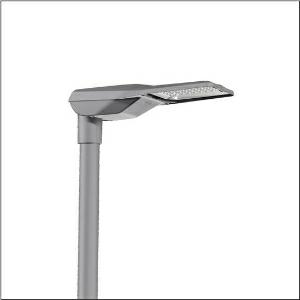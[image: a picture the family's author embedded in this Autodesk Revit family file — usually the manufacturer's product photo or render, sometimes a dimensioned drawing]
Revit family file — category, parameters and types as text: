
# Revit family: streetlight_sl_21_iq_mini___st1_5a_5xe2p41d08hb_72ee
name_source: partatom
category: Lighting Fixtures
units: mm (PartAtom-declared; Revit-internal decimal feet)

## family parameters
Cut with Voids When Loaded = No
Host = Face
Light Source = No
Part Type = Normal
Room Calculation Point = No
Round Connector Dimension = Use Diameter
Shared = No

## types (1)
- --- (1 x LED, 9690 lm, 70.9 W, 4000K)
    Apparent Load = 71 VA
    CIE Flux Codes = 22 53 95 100 100
    Color Rendering = 70
    Color Temperature = 4000K
    Default Elevation = 1800 mm
    Description = Streetlight SL 21 mini, mast luminaire, primary light control with lens, of PMMA, primary optical cover: cover, of toughened safety glass, transparent, light distribution: ST1.5a, light emission: direct distribution, primary light characteristic: asymmetric, installation type: post-top, side-entry, LED, High Power LED, rated luminous flux: 9.690lm, luminous efficacy: 137lm/W, light colour: 740, colour temperature: 4000K, control gear: ECG iQ, control: Auto-Match, Temp-Guard, Lumen-Switch, Night-Set, Smart-Wire, Light-Fading, Desk-Remote (wireless, voltage-free reading and setting of iQ features in the workshop via application-optimized NFC function/RFID function), optimised constant luminous flux control (CLO 2.0), mains connection: 220..240V, AC, 50/60Hz, start of lifetime: 71W, end of lifetime: 75W, reduction: 31W, luminaire housing, of diecast aluminium, powder-coated, Siteco® metallic grey (DB 702S), corrosivity category C5 according to DIN EN ISO 12944, length: 628mm, width: 235mm, height: 110mm, spigot size: 60/76mm (post-top) and 42/60/76mm (side-entry), mast flange for spigot size: 42mm: 5XC10008XM4, 60mm: 5XC10008XM2, 76/60mm: 5XC10108XM1, protection rating (complete): IP66, insulation class (complete): insulation class II (safety insulation), certification: CE, ENEC, VDE, impact resistance: IK09, permissible operating ambient temperature for outdoor applications: -40..+50°C, standard-compliant lighting for roads and squares, packaging unit: 1 piece

Light Distribution: ST1.5a
    Height = 110 mm
    Lamp = 1 x LED
    Lamp Light Flux = 9690 lm
    Lamp Power = 70.9 W
    Lamp count = 1
    Length = 625 mm
    Luminous efficacy = 137 lm/W
    Manufacturer = Siteco
    ModVariant = No
    Model = 5XE2P41D08HB
    Number of Poles = 1
    OnlyDefault = Yes
    Power Factor = 1
    Product Name = Streetlight SL 21 iQ mini | ST1.5a
    Product group = mast luminaire | pylon top
    ProductGroupID = 6100
    Protection Class = Protection class II
    Protection Degree = IP 66
    RLX_Detail_Level = 1
    RlxData = <blob elided: 95889 chars, md5=a17f6273>
    Socket = socket
    Standby Power = 0 W
    System Light Flux = 9690 lm
    System Power = 71 W
    Type Comments = factory setting: luminous flux: 100 % | dim-lin: 254 | 711 mA
    Type Image = l_1003519.jpg
    URL = http://relux.com
    VarID = @adj_068353
    Voltage = 0 V
    Weight = 0.00 kg
    Width = 234 mm

## geometry (parser evidence)
native form markers: Blend x4, Sweep x11
no freeform markers — native parametric forms only
